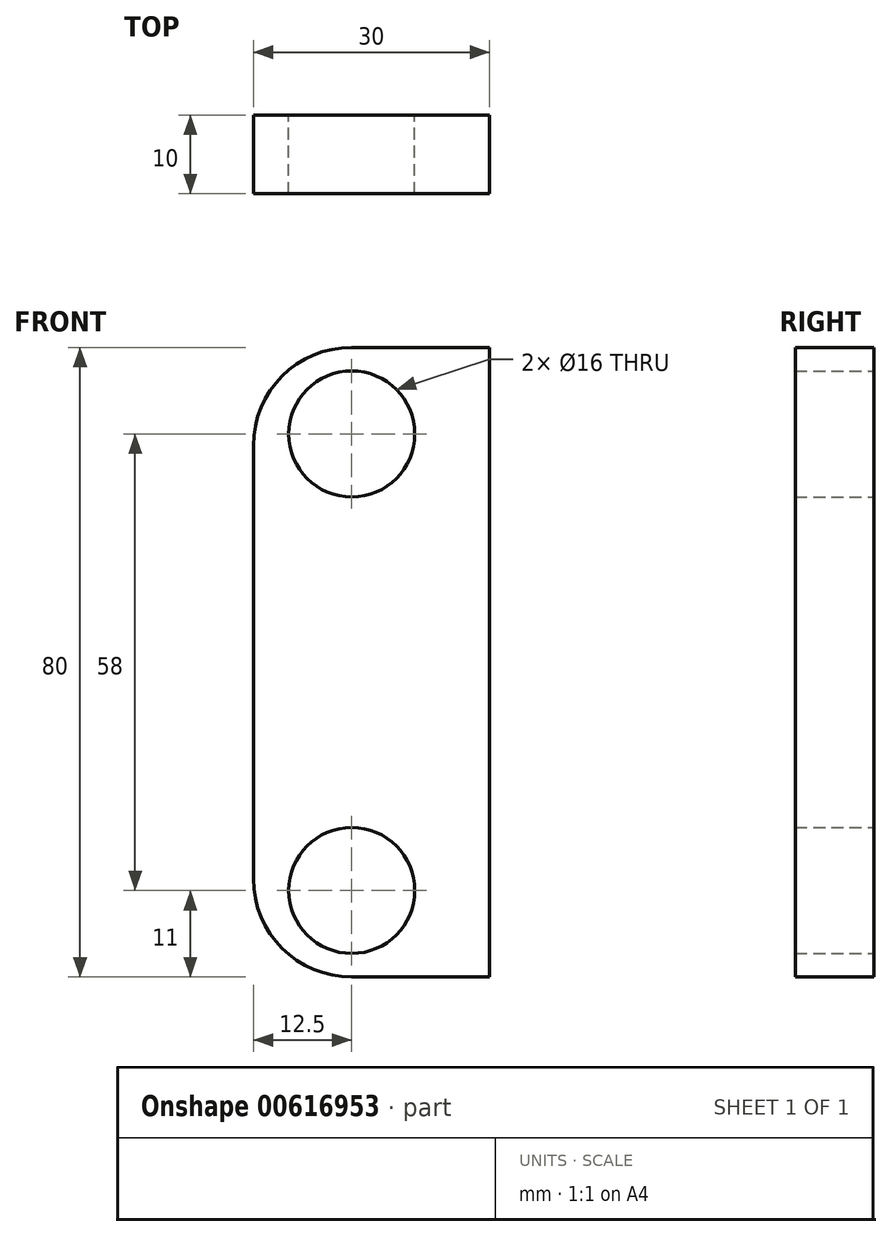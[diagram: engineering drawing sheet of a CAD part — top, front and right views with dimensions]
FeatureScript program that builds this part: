
annotation { "Feature Type Name" : "Feature", "Feature Type Description" : "" }
export const myFeature = defineFeature(function(context is Context, id is Id, definition is map)
    precondition{}
    {
        {
            var Q0;
            Q0=qCreatedBy(makeId("Front.planeOp"),FACE);
            var sketch = newSketch(context, id + "F0", { "sketchPlane" : qUnion([Q0])});
            skLineSegment(sketch, "E0.bottom", {"start": v(15, -40) * mm, "end": v(-2.5, -40) * mm});
            skLineSegment(sketch, "E0.top", {"start": v(15, 40) * mm, "end": v(-2.5, 40) * mm});
            skLineSegment(sketch, "E0.left", {"start": v(15, -40) * mm, "end": v(15, 40) * mm});
            skLineSegment(sketch, "E0.right", {"start": v(-15, -27.5) * mm, "end": v(-15, 27.5) * mm});
            skPoint(sketch, "E0.middle", {"position": v(0, 0) * mm});
            skLineSegment(sketch, "E1", {"start": v(-15, 29) * mm, "end": v(15, 29) * mm});
            skLineSegment(sketch, "E2", {"start": v(-15, -29) * mm, "end": v(15, -29) * mm});
            skLineSegment(sketch, "E3", {"start": v(-2.5, 40) * mm, "end": v(-2.5, -40) * mm});
            skPoint(sketch, "E3.endSnap0", {"position": v(0, -40) * mm});
            skPoint(sketch, "E4", {"position": v(-2.5, 29) * mm});
            skPoint(sketch, "E5", {"position": v(-2.5, -29) * mm});
            skCircle(sketch, "E6", {"center": v(-2.5, 29) * mm, "radius": 8 * mm});
            skCircle(sketch, "E7", {"center": v(-2.5, -29) * mm, "radius": 8 * mm});
            skPoint(sketch, "E8.visualSharp", {"position": v(-15, 40) * mm});
            skArc(sketch, "E8.filletArc", {"start": v(-2.5, 40) * mm, "mid": v(-11.34, 36.34) * mm, "end": v(-15, 27.5) * mm});
            skPoint(sketch, "E9.visualSharp", {"position": v(-15, -40) * mm});
            skArc(sketch, "E9.filletArc", {"start": v(-15, -27.5) * mm, "mid": v(-11.34, -36.34) * mm, "end": v(-2.5, -40) * mm});
            skSolve(sketch);
        }
        {
            var Q0;
            Q0 = qSketchRegion(id + "F0", true);
            extrude(context, id + "F1", {"entities" : qUnion([Q0]), "depth" : 10 * mm, "offsetDistance" : 25 * mm});
        }
    });
